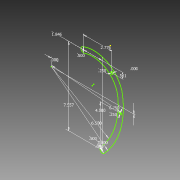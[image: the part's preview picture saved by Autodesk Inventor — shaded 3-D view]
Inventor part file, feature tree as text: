
AUTODESK INVENTOR PART (.ipt)
format: ipt  version: 2012 (Build 160160000, 160)  size: 78,336 bytes
history: native  units: in
note: dims shown in document units (in); Inventor stores cm internally (conversion verified against a paired STEP export)
features: sketch x1
ambient origin geometry x8: Origin, YZ Plane, XZ Plane, XY Plane, X Axis, Y Axis, Z Axis, Center Point
feature tree (1):
  sketch  "Sketch1"  dims[d0=0.0in d1=7.0in d2=6.5in d3=0.0in d5=0.5in d6=0.0in d7=0.5in d9=0.25in d10=0.25in d11=6.75in d12=4.0in d13=7.5571in d14=1.8463in d15=2.7757in d16=0.5608in]
